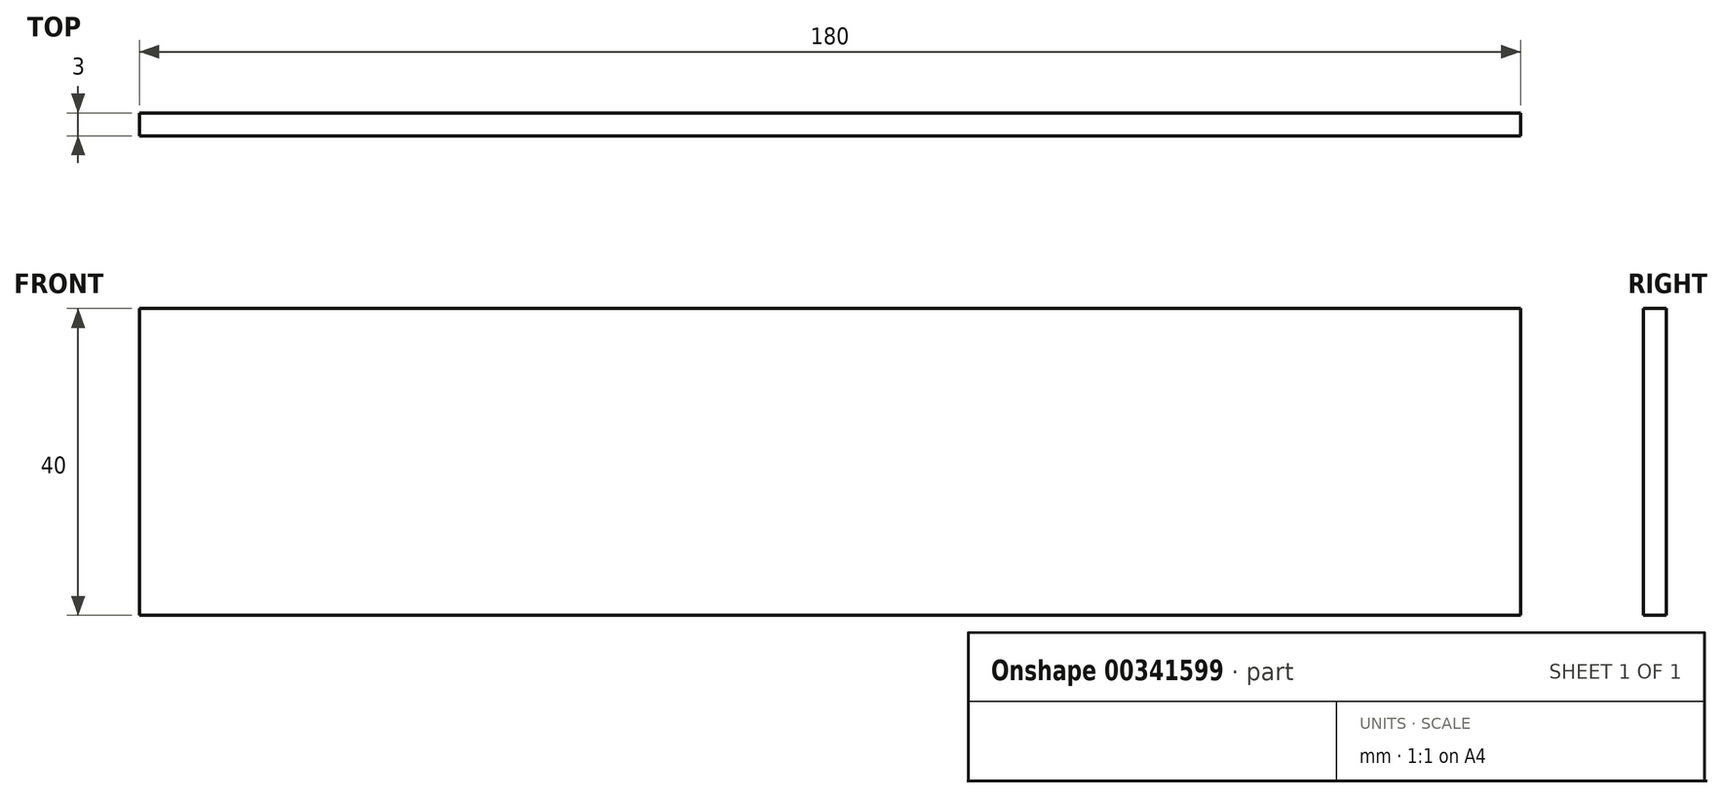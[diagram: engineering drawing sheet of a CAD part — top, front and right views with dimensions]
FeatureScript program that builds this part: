
annotation { "Feature Type Name" : "Feature", "Feature Type Description" : "" }
export const myFeature = defineFeature(function(context is Context, id is Id, definition is map)
    precondition{}
    {
        {
            var Q0;
            Q0=qCreatedBy(makeId("Top.planeOp"),FACE);
            var sketch = newSketch(context, id + "F0", { "sketchPlane" : qUnion([Q0])});
            skLineSegment(sketch, "E0.bottom", {"start": v(-67.43, -41.78) * mm, "end": v(112.57, -41.78) * mm});
            skLineSegment(sketch, "E0.top", {"start": v(-67.43, -44.78) * mm, "end": v(112.57, -44.78) * mm});
            skLineSegment(sketch, "E0.left", {"start": v(-67.43, -41.78) * mm, "end": v(-67.43, -44.78) * mm});
            skLineSegment(sketch, "E0.right", {"start": v(112.57, -41.78) * mm, "end": v(112.57, -44.78) * mm});
            skSolve(sketch);
        }
        {
            var Q0;
            Q0=makeQuery(id+"F0.imprint","IMPRINT",FACE,{"disambiguationData":[TD([[makeQuery(id+"F0.imprint","IMPRINT",EDGE,{"derivedFrom":sQuery(id+"F0.wireOp",EDGE,"E0.bottom")}),-1.0]])]});
            extrude(context, id + "F1", {"entities" : qUnion([Q0]), "depth" : 40 * mm});
        }
    });
